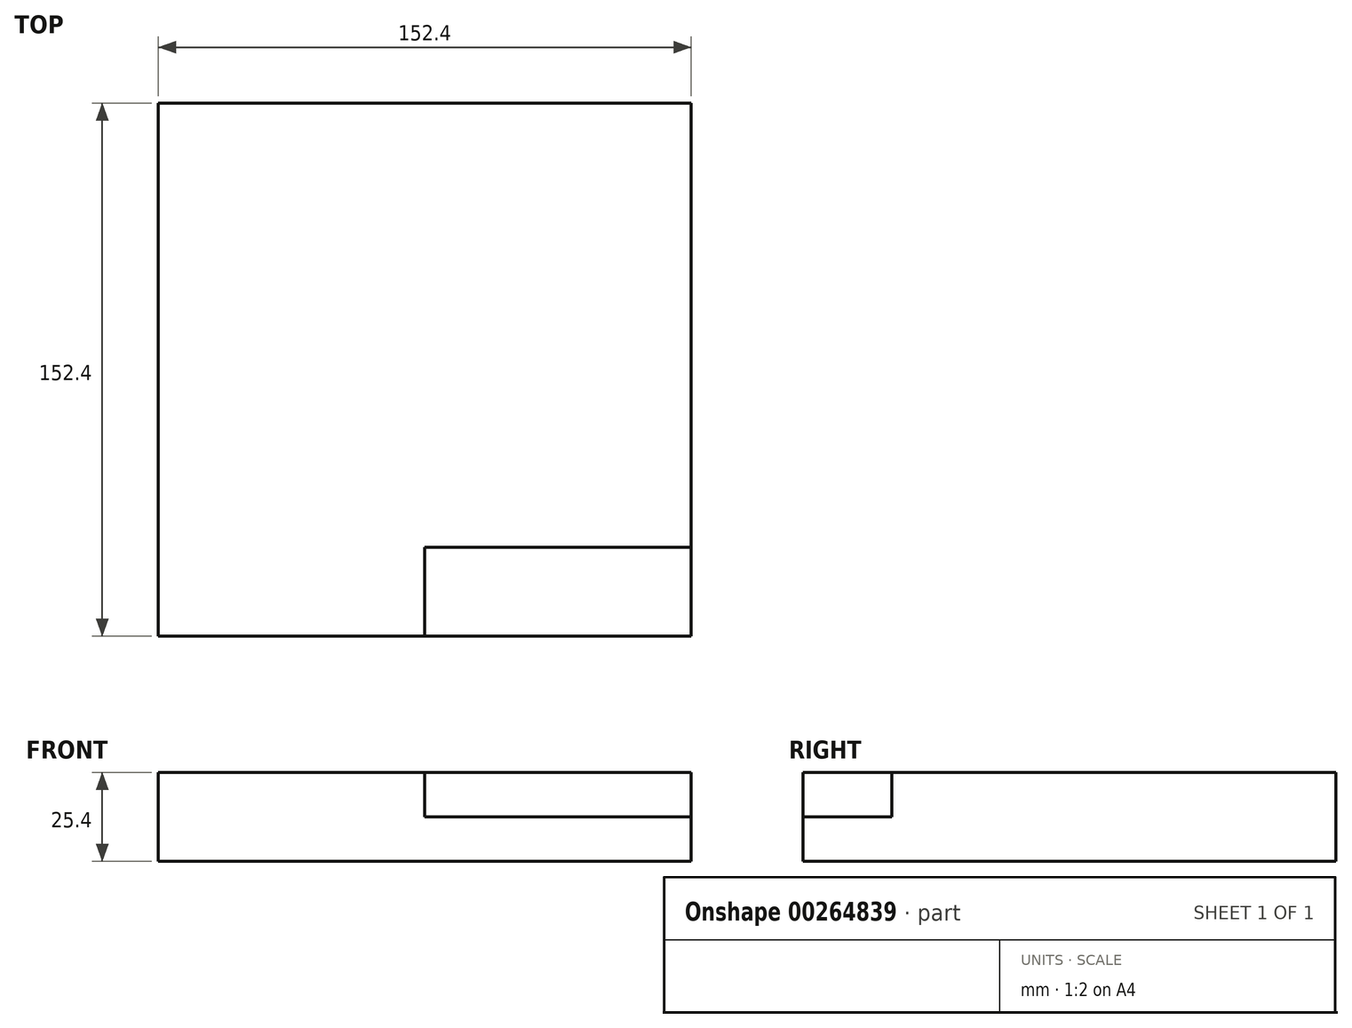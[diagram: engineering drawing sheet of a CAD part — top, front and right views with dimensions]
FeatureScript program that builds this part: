
annotation { "Feature Type Name" : "Feature", "Feature Type Description" : "" }
export const myFeature = defineFeature(function(context is Context, id is Id, definition is map)
    precondition{}
    {
        {
            var Q0;
            Q0=qCreatedBy(makeId("Top.planeOp"),FACE);
            var sketch = newSketch(context, id + "F0", { "sketchPlane" : qUnion([Q0])});
            skLineSegment(sketch, "E0.bottom", {"start": v(0, 0) * mm, "end": v(152.4, 0) * mm});
            skLineSegment(sketch, "E0.top", {"start": v(0, 152.4) * mm, "end": v(152.4, 152.4) * mm});
            skLineSegment(sketch, "E0.left", {"start": v(0, 0) * mm, "end": v(0, 152.4) * mm});
            skLineSegment(sketch, "E0.right", {"start": v(152.4, 0) * mm, "end": v(152.4, 152.4) * mm});
            skSolve(sketch);
        }
        {
            var Q0;
            Q0=makeQuery(id+"F0.imprint","IMPRINT",FACE,{"disambiguationData":[TD([[makeQuery(id+"F0.imprint","IMPRINT",EDGE,{"derivedFrom":sQuery(id+"F0.wireOp",EDGE,"E0.bottom")}),1.0]])]});
            extrude(context, id + "F1", {"entities" : qUnion([Q0]), "depth" : 25.4 * mm});
        }
        {
            var Q0;
            Q0=makeQuery(id+"F1.opExtrude","SWEPT_FACE",FACE,{"disambiguationData":[OSD([sQuery(id+"F0.wireOp",EDGE,"E0.bottom")])]});
            var sketch = newSketch(context, id + "F2", { "sketchPlane" : qUnion([Q0])});
            skLineSegment(sketch, "E1.bottom", {"start": v(152.4, 25.4) * mm, "end": v(76.2, 25.4) * mm});
            skLineSegment(sketch, "E1.top", {"start": v(152.4, 12.7) * mm, "end": v(76.2, 12.7) * mm});
            skLineSegment(sketch, "E1.left", {"start": v(152.4, 25.4) * mm, "end": v(152.4, 12.7) * mm});
            skLineSegment(sketch, "E1.right", {"start": v(76.2, 25.4) * mm, "end": v(76.2, 12.7) * mm});
            skSolve(sketch);
        }
        {
            var Q0;
            Q0=makeQuery(id+"F2.imprint","IMPRINT",FACE,{"disambiguationData":[TD([[makeQuery(id+"F2.imprint","IMPRINT",EDGE,{"derivedFrom":sQuery(id+"F2.wireOp",EDGE,"E1.bottom")}),-1.0]])]});
            var Q1;
            Q1=makeQuery(id+"F1.opExtrude","SWEPT_FACE",FACE,{"disambiguationData":[OSD([sQuery(id+"F0.wireOp",EDGE,"E0.top")])]});
            extrude(context, id + "F3", {"entities" : qUnion([Q0, Q1]), "operationType" : NewBodyOperationType.REMOVE, "oppositeDirection" : true, "depth" : 25.4 * mm});
        }
    });
